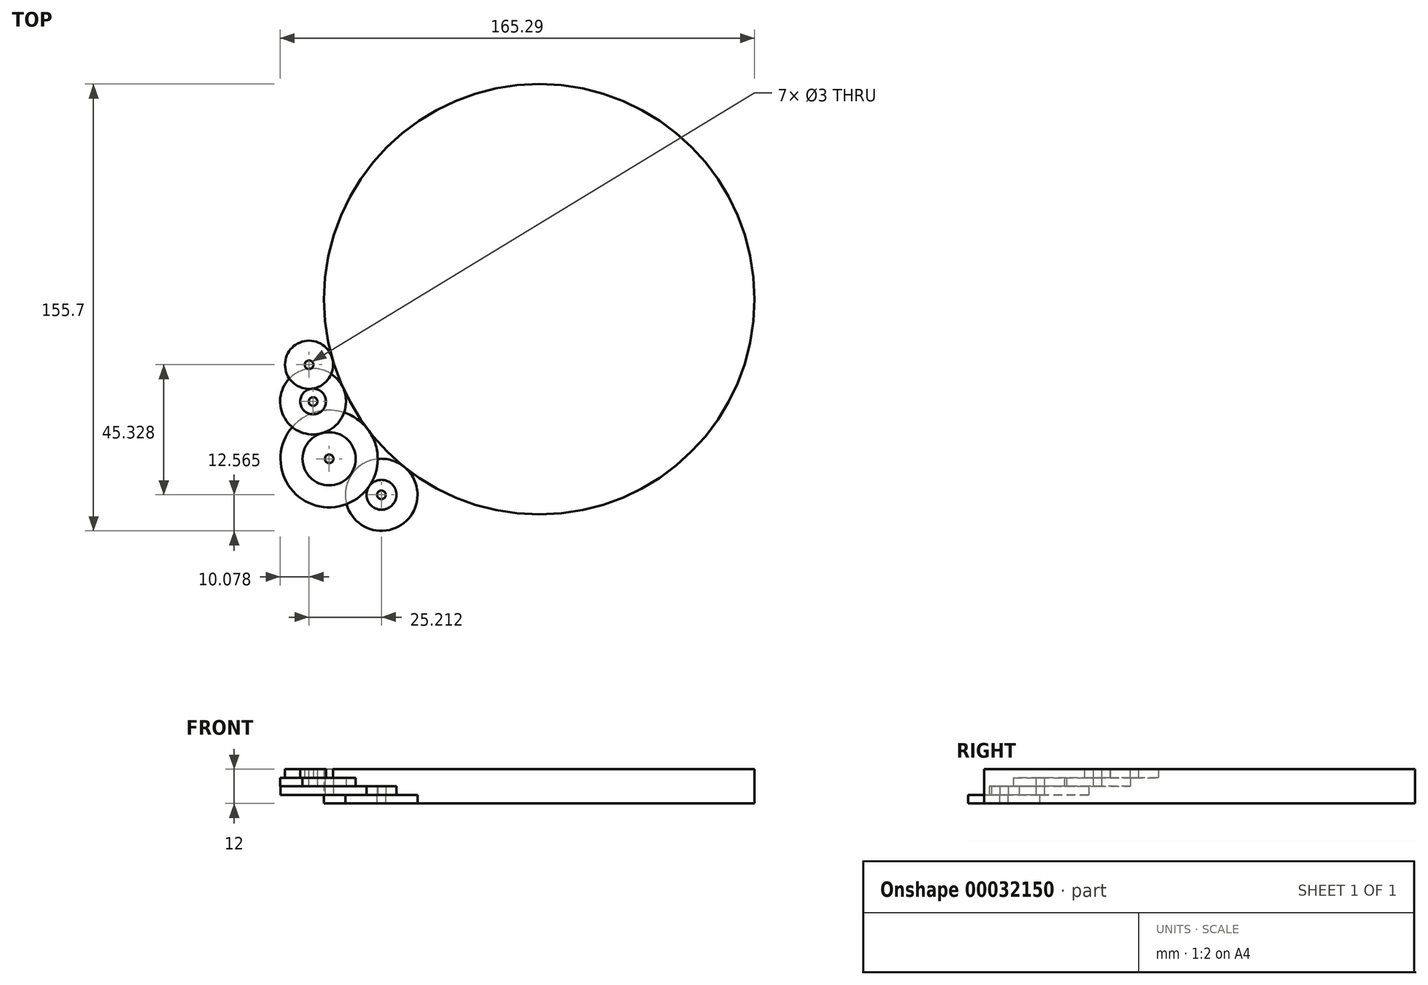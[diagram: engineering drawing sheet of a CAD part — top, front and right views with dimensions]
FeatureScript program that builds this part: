
annotation { "Feature Type Name" : "Feature", "Feature Type Description" : "" }
export const myFeature = defineFeature(function(context is Context, id is Id, definition is map)
    precondition{}
    {
        {
            var Q0;
            Q0=qCreatedBy(makeId("Top.planeOp"),FACE);
            var sketch = newSketch(context, id + "F0", { "sketchPlane" : qUnion([Q0])});
            skCircle(sketch, "E0", {"center": v(0, 0) * mm, "radius": 75 * mm});
            skSolve(sketch);
        }
        {
            var Q0;
            Q0 = qSketchRegion(id + "F0", true);
            extrude(context, id + "F1", {"entities" : qUnion([Q0]), "depth" : 9 * mm});
        }
        {
            var Q0;
            Q0=qCreatedBy(makeId("Top.planeOp"),FACE);
            var sketch = newSketch(context, id + "F2", { "sketchPlane" : qUnion([Q0])});
            skCircle(sketch, "E1.0", {"center": v(0, 0) * mm, "radius": 75 * mm, "construction": true});
            skCircle(sketch, "E2", {"center": v(-73.22, -55.58) * mm, "radius": 16.93 * mm});
            skCircle(sketch, "E3", {"center": v(-73.22, -55.58) * mm, "radius": 1.5 * mm});
            skSolve(sketch);
        }
        {
            var Q0;
            Q0 = qSketchRegion(id + "F2", true);
            extrude(context, id + "F3", {"entities" : qUnion([Q0]), "operationType" : NewBodyOperationType.ADD, "depth" : 3 * mm});
        }
        {
            var Q0;
            Q0=makeQuery(id+"F3.opExtrude","CAP_FACE",FACE,{"disambiguationData":[OSD([sQuery(id+"F2.wireOp",EDGE,"E2")])],"isStart":false});
            var sketch = newSketch(context, id + "F4", { "sketchPlane" : qUnion([Q0])});
            skCircle(sketch, "E4.0.0", {"center": v(-73.22, -55.58) * mm, "radius": 16.93 * mm, "construction": true});
            skCircle(sketch, "E5", {"center": v(-73.22, -55.58) * mm, "radius": 9.25 * mm});
            skCircle(sketch, "E6.0.0", {"center": v(0, 0) * mm, "radius": 75 * mm, "construction": true});
            skCircle(sketch, "E7", {"center": v(-78.81, -35.6) * mm, "radius": 11.48 * mm});
            skCircle(sketch, "E8.0", {"center": v(-73.22, -55.58) * mm, "radius": 1.5 * mm});
            skCircle(sketch, "E9", {"center": v(-78.81, -35.6) * mm, "radius": 1.5 * mm});
            skSolve(sketch);
        }
        {
            var Q0;
            Q0 = qSketchRegion(id + "F4", true);
            extrude(context, id + "F5", {"entities" : qUnion([Q0]), "depth" : 3 * mm});
        }
        {
            var Q0;
            Q0=makeQuery(id+"F5.opExtrude","CAP_FACE",FACE,{"disambiguationData":[OSD([sQuery(id+"F4.wireOp",EDGE,"E7")])],"isStart":false});
            var sketch = newSketch(context, id + "F6", { "sketchPlane" : qUnion([Q0])});
            skCircle(sketch, "E10.0.0", {"center": v(-78.81, -35.6) * mm, "radius": 11.48 * mm, "construction": true});
            skCircle(sketch, "E11", {"center": v(-78.81, -35.6) * mm, "radius": 4.49 * mm});
            skCircle(sketch, "E12.0", {"center": v(0, 0) * mm, "radius": 75 * mm, "construction": true});
            skCircle(sketch, "E13", {"center": v(-80.21, -22.8) * mm, "radius": 8.4 * mm});
            skCircle(sketch, "E14.0", {"center": v(-78.81, -35.6) * mm, "radius": 1.5 * mm});
            skCircle(sketch, "E15", {"center": v(-80.21, -22.8) * mm, "radius": 1.5 * mm});
            skSolve(sketch);
        }
        {
            var Q0;
            Q0 = qSketchRegion(id + "F6", true);
            extrude(context, id + "F7", {"entities" : qUnion([Q0]), "depth" : 3 * mm});
        }
        {
            var Q0;
            Q0=makeQuery(id+"F1.opExtrude","CAP_FACE",FACE,{"disambiguationData":[OSD([sQuery(id+"F0.wireOp",EDGE,"E0")])],"isStart":true});
            var sketch = newSketch(context, id + "F8", { "sketchPlane" : qUnion([Q0])});
            skCircle(sketch, "E16.0.0", {"center": v(0, 0) * mm, "radius": 75 * mm});
            skSolve(sketch);
        }
        {
            var Q0;
            Q0 = qSketchRegion(id + "F8", true);
            extrude(context, id + "F9", {"entities" : qUnion([Q0]), "operationType" : NewBodyOperationType.ADD, "depth" : 3 * mm});
        }
        {
            var Q0;
            Q0=qCreatedBy(makeId("Top.planeOp"),FACE);
            var sketch = newSketch(context, id + "F10", { "sketchPlane" : qUnion([Q0])});
            skCircle(sketch, "E17.0", {"center": v(-73.22, -55.58) * mm, "radius": 16.93 * mm, "construction": true});
            skCircle(sketch, "E18.0", {"center": v(0, 0) * mm, "radius": 75 * mm, "construction": true});
            skCircle(sketch, "E19", {"center": v(-55, -68.13) * mm, "radius": 5.2 * mm});
            skCircle(sketch, "E20", {"center": v(-55, -68.13) * mm, "radius": 1.5 * mm});
            skSolve(sketch);
        }
        {
            var Q0;
            Q0 = qSketchRegion(id + "F10", true);
            extrude(context, id + "F11", {"entities" : qUnion([Q0]), "operationType" : NewBodyOperationType.ADD, "depth" : 3 * mm});
        }
        {
            var Q0;
            Q0=qCreatedBy(makeId("Top.planeOp"),FACE);
            var sketch = newSketch(context, id + "F12", { "sketchPlane" : qUnion([Q0])});
            skCircle(sketch, "E21.0.0", {"center": v(-55, -68.13) * mm, "radius": 5.2 * mm, "construction": true});
            skCircle(sketch, "E22", {"center": v(-55, -68.13) * mm, "radius": 12.56 * mm});
            skCircle(sketch, "E23.0", {"center": v(0, 0) * mm, "radius": 75 * mm, "construction": true});
            skCircle(sketch, "E24.0", {"center": v(-55, -68.13) * mm, "radius": 1.5 * mm});
            skSolve(sketch);
        }
        {
            var Q0;
            Q0 = qSketchRegion(id + "F12", true);
            extrude(context, id + "F13", {"entities" : qUnion([Q0]), "oppositeDirection" : true, "depth" : 3 * mm});
        }
    });
